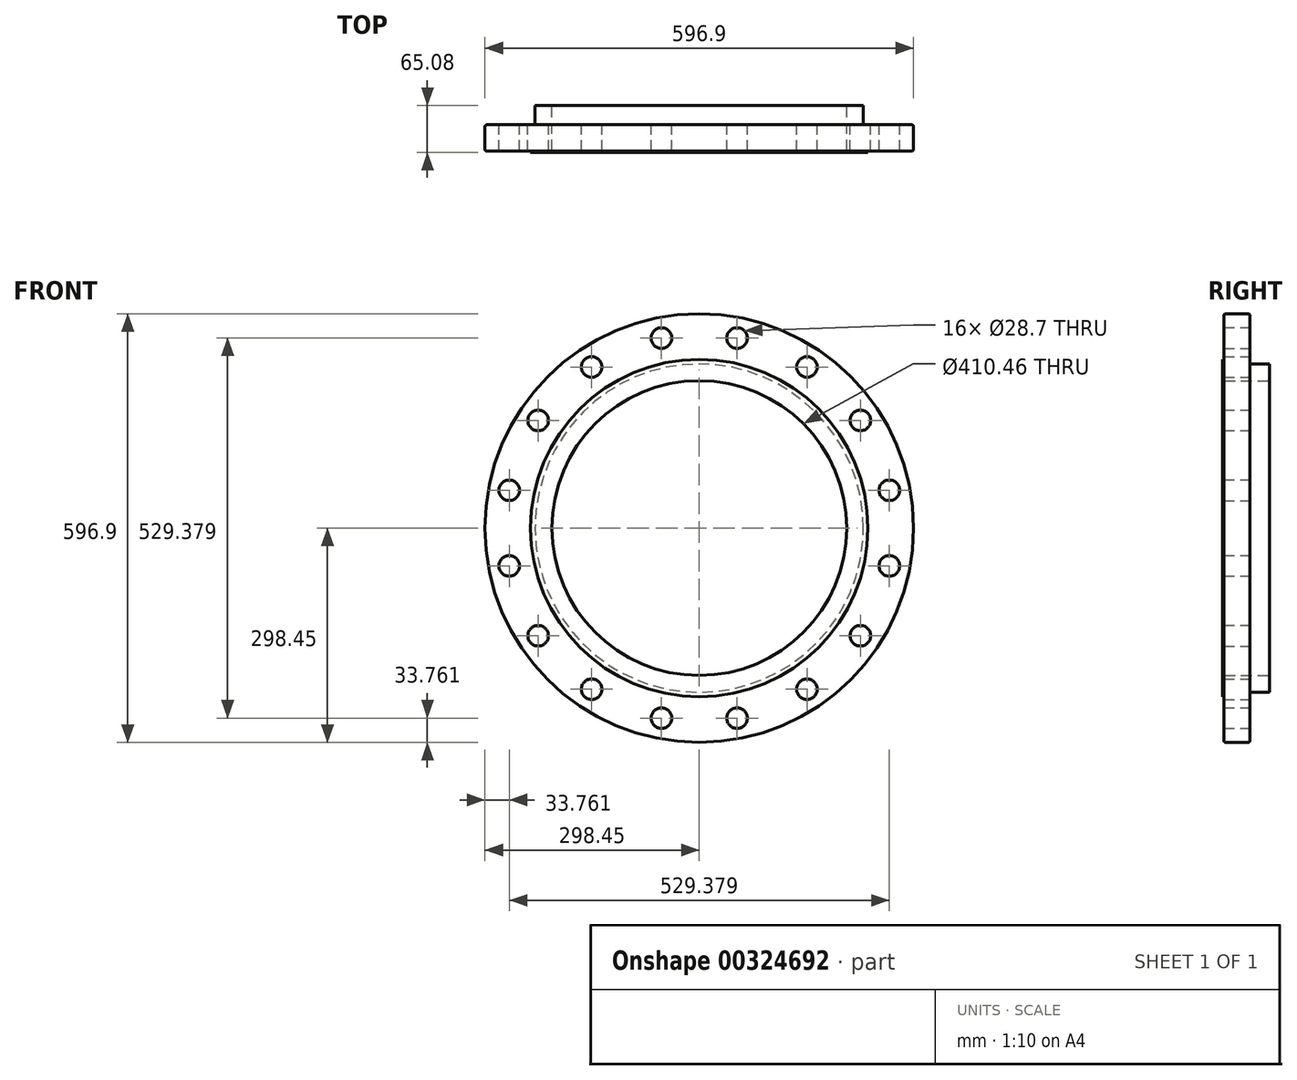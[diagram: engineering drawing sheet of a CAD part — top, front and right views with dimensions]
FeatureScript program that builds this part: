
annotation { "Feature Type Name" : "Feature", "Feature Type Description" : "" }
export const myFeature = defineFeature(function(context is Context, id is Id, definition is map)
    precondition{}
    {
        {
            var Q0;
            Q0=qCreatedBy(makeId("Front.planeOp"),FACE);
            var sketch = newSketch(context, id + "F0", { "sketchPlane" : qUnion([Q0])});
            skCircle(sketch, "E0", {"center": v(0, 0) * mm, "radius": 298.45 * mm});
            skCircle(sketch, "E1", {"center": v(0, 0) * mm, "radius": 205.23 * mm});
            skCircle(sketch, "E2", {"center": v(52.65, 264.69) * mm, "radius": 14.35 * mm});
            skCircle(sketch, "E3.1.0", {"center": v(-52.65, 264.69) * mm, "radius": 14.35 * mm});
            skCircle(sketch, "E3.2.0", {"center": v(-149.93, 224.4) * mm, "radius": 14.35 * mm});
            skCircle(sketch, "E3.3.0", {"center": v(-224.4, 149.93) * mm, "radius": 14.35 * mm});
            skCircle(sketch, "E3.4.0", {"center": v(-264.69, 52.65) * mm, "radius": 14.35 * mm});
            skCircle(sketch, "E3.5.0", {"center": v(-264.69, -52.65) * mm, "radius": 14.35 * mm});
            skCircle(sketch, "E3.6.0", {"center": v(-224.4, -149.93) * mm, "radius": 14.35 * mm});
            skCircle(sketch, "E3.7.0", {"center": v(-149.93, -224.4) * mm, "radius": 14.35 * mm});
            skCircle(sketch, "E3.8.0", {"center": v(-52.65, -264.69) * mm, "radius": 14.35 * mm});
            skCircle(sketch, "E3.9.0", {"center": v(52.65, -264.69) * mm, "radius": 14.35 * mm});
            skCircle(sketch, "E3.10.0", {"center": v(149.93, -224.4) * mm, "radius": 14.35 * mm});
            skCircle(sketch, "E3.11.0", {"center": v(224.4, -149.93) * mm, "radius": 14.35 * mm});
            skCircle(sketch, "E3.12.0", {"center": v(264.69, -52.65) * mm, "radius": 14.35 * mm});
            skCircle(sketch, "E3.13.0", {"center": v(264.69, 52.65) * mm, "radius": 14.35 * mm});
            skCircle(sketch, "E3.14.0", {"center": v(224.4, 149.93) * mm, "radius": 14.35 * mm});
            skCircle(sketch, "E3.15.0", {"center": v(149.93, 224.4) * mm, "radius": 14.35 * mm});
            skSolve(sketch);
        }
        {
            var Q0;
            Q0=makeQuery(id+"F0.imprint","IMPRINT",FACE,{"disambiguationData":[TD([[makeQuery(id+"F0.imprint","IMPRINT",EDGE,{"derivedFrom":sQuery(id+"F0.wireOp",EDGE,"E0")}),1.0]])]});
            extrude(context, id + "F1", {"entities" : qUnion([Q0]), "depth" : 36.58 * mm});
        }
        {
            var Q0;
            Q0=makeQuery(id+"F1.opExtrude","CAP_FACE",FACE,{"disambiguationData":[OSD([sQuery(id+"F0.wireOp",EDGE,"E0"),sQuery(id+"F0.wireOp",EDGE,"E1"),sQuery(id+"F0.wireOp",EDGE,"E2"),sQuery(id+"F0.wireOp",EDGE,"E3.1.0"),sQuery(id+"F0.wireOp",EDGE,"E3.2.0"),sQuery(id+"F0.wireOp",EDGE,"E3.3.0"),sQuery(id+"F0.wireOp",EDGE,"E3.4.0"),sQuery(id+"F0.wireOp",EDGE,"E3.5.0"),sQuery(id+"F0.wireOp",EDGE,"E3.6.0"),sQuery(id+"F0.wireOp",EDGE,"E3.7.0"),sQuery(id+"F0.wireOp",EDGE,"E3.8.0"),sQuery(id+"F0.wireOp",EDGE,"E3.9.0"),sQuery(id+"F0.wireOp",EDGE,"E3.10.0"),sQuery(id+"F0.wireOp",EDGE,"E3.11.0"),sQuery(id+"F0.wireOp",EDGE,"E3.12.0"),sQuery(id+"F0.wireOp",EDGE,"E3.13.0"),sQuery(id+"F0.wireOp",EDGE,"E3.14.0"),sQuery(id+"F0.wireOp",EDGE,"E3.15.0")])],"isStart":false});
            var sketch = newSketch(context, id + "F2", { "sketchPlane" : qUnion([Q0])});
            skCircle(sketch, "E4", {"center": v(0, 0) * mm, "radius": 234.95 * mm});
            skCircle(sketch, "E5", {"center": v(0, 0) * mm, "radius": 205.23 * mm});
            skSolve(sketch);
        }
        {
            var Q0;
            Q0=makeQuery(id+"F2.imprint","IMPRINT",FACE,{"disambiguationData":[TD([[makeQuery(id+"F2.imprint","IMPRINT",EDGE,{"derivedFrom":sQuery(id+"F2.wireOp",EDGE,"E4")}),1.0]])]});
            extrude(context, id + "F3", {"entities" : qUnion([Q0]), "operationType" : NewBodyOperationType.ADD, "depth" : 1.59 * mm});
        }
        {
            var Q0;
            Q0=makeQuery(id+"F1.opExtrude","CAP_FACE",FACE,{"disambiguationData":[OSD([sQuery(id+"F0.wireOp",EDGE,"E0"),sQuery(id+"F0.wireOp",EDGE,"E1"),sQuery(id+"F0.wireOp",EDGE,"E2"),sQuery(id+"F0.wireOp",EDGE,"E3.1.0"),sQuery(id+"F0.wireOp",EDGE,"E3.2.0"),sQuery(id+"F0.wireOp",EDGE,"E3.3.0"),sQuery(id+"F0.wireOp",EDGE,"E3.4.0"),sQuery(id+"F0.wireOp",EDGE,"E3.5.0"),sQuery(id+"F0.wireOp",EDGE,"E3.6.0"),sQuery(id+"F0.wireOp",EDGE,"E3.7.0"),sQuery(id+"F0.wireOp",EDGE,"E3.8.0"),sQuery(id+"F0.wireOp",EDGE,"E3.9.0"),sQuery(id+"F0.wireOp",EDGE,"E3.10.0"),sQuery(id+"F0.wireOp",EDGE,"E3.11.0"),sQuery(id+"F0.wireOp",EDGE,"E3.12.0"),sQuery(id+"F0.wireOp",EDGE,"E3.13.0"),sQuery(id+"F0.wireOp",EDGE,"E3.14.0"),sQuery(id+"F0.wireOp",EDGE,"E3.15.0")])],"isStart":true});
            var sketch = newSketch(context, id + "F4", { "sketchPlane" : qUnion([Q0])});
            skCircle(sketch, "E6", {"center": v(0, 0) * mm, "radius": 228.6 * mm});
            skCircle(sketch, "E7", {"center": v(0, 0) * mm, "radius": 205.23 * mm});
            skSolve(sketch);
        }
        {
            var Q0;
            Q0 = qSketchRegion(id + "F4", true);
            extrude(context, id + "F5", {"entities" : qUnion([Q0]), "operationType" : NewBodyOperationType.ADD, "depth" : 26.92 * mm});
        }
        {
            var Q0;
            Q0=makeQuery(id+"F1.opExtrude","CAP_EDGE",EDGE,{"disambiguationData":[OSD([sQuery(id+"F0.wireOp",EDGE,"E0")])],"isStart":true});
            var Q1;
            Q1=makeQuery(id+"F5.opExtrude","CAP_EDGE",EDGE,{"disambiguationData":[OSD([sQuery(id+"F4.wireOp",EDGE,"E7")])],"isStart":false});
            var Q2;
            Q2=makeQuery(id+"F1.opExtrude","CAP_EDGE",EDGE,{"disambiguationData":[OSD([sQuery(id+"F0.wireOp",EDGE,"E0")])],"isStart":false});
            var Q3;
            Q3=makeQuery(id+"F3.opExtrude","CAP_EDGE",EDGE,{"disambiguationData":[OSD([sQuery(id+"F2.wireOp",EDGE,"E5")])],"isStart":false});
            fillet(context, id + "F6", {"entities" : qUnion([Q0, Q1, Q2, Q3]), "radius" : 2.54 * mm, "tangentPropagation" : true, "allowEdgeOverflow" : false});
        }
    });
